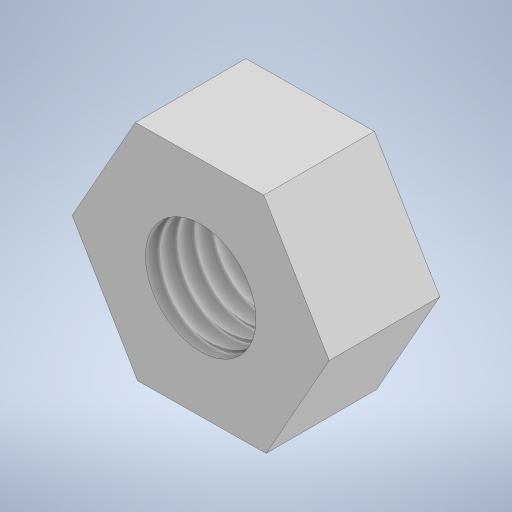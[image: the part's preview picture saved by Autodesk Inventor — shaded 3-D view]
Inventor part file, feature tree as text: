
AUTODESK INVENTOR PART (.ipt)
format: ipt  version: 2024 (Build 280153000, 153)  size: 220,160 bytes
history: native  units: mm
features: extrude x2, sketch x2, thread x1
ambient origin geometry x8: Origin, YZ Plane, XZ Plane, XY Plane, X Axis, Y Axis, Z Axis, Center Point
bodies: Solid1 (feature_tree)
feature tree (5):
  extrude  "Extrusion1"  Depth=5.0mm TaperAngle=0.0deg
  extrude  "Extrusion2"  Depth=5.0mm TaperAngle=0.0deg
  thread  "Thread1"  [1 undecoded]
  sketch  "Sketch1"  dims[d0=10.0mm d1=5.0mm d2=0.0mm]
  sketch  "Sketch2"  dims[d3=5.0mm d4=12.5mm d5=0.0mm d6=5.0mm d7=0.0mm]
note: 1 required parameter value undecoded (feature->parameter linkage not recoverable at this tier; creation-order binding heuristic only, values carry confidence <= 0.55)
